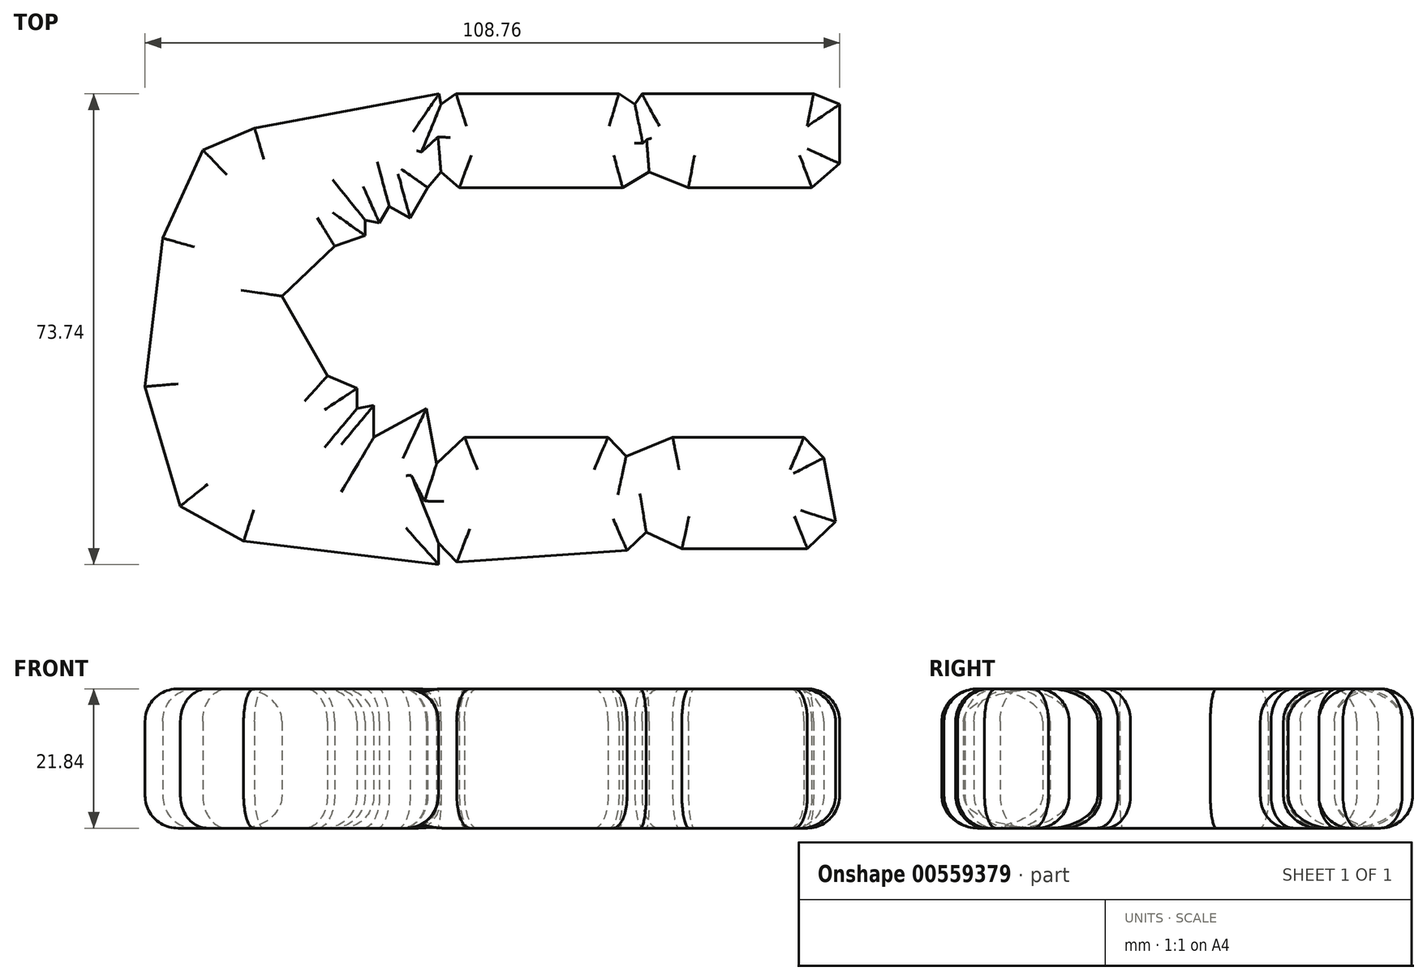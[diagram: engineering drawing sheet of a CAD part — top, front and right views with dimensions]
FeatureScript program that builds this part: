
annotation { "Feature Type Name" : "Feature", "Feature Type Description" : "" }
export const myFeature = defineFeature(function(context is Context, id is Id, definition is map)
    precondition{}
    {
        {
            var Q0;
            Q0=qCreatedBy(makeId("Top.planeOp"),FACE);
            var sketch = newSketch(context, id + "F0", { "sketchPlane" : qUnion([Q0])});
            skLineSegment(sketch, "E0", {"start": v(-56.88, -14.18) * mm, "end": v(-54.1, 9.09) * mm});
            skLineSegment(sketch, "E1", {"start": v(-54.1, 9.09) * mm, "end": v(-47.85, 22.91) * mm});
            skLineSegment(sketch, "E2", {"start": v(-47.85, 22.91) * mm, "end": v(-39.72, 26.3) * mm});
            skLineSegment(sketch, "E3", {"start": v(-39.72, 26.3) * mm, "end": v(-10.85, 31.7) * mm});
            skLineSegment(sketch, "E4", {"start": v(-10.85, 31.7) * mm, "end": v(-10.54, 30.04) * mm});
            skLineSegment(sketch, "E5", {"start": v(-10.54, 30.04) * mm, "end": v(-8.16, 31.7) * mm});
            skLineSegment(sketch, "E6", {"start": v(-8.16, 31.7) * mm, "end": v(17.31, 31.7) * mm});
            skLineSegment(sketch, "E7", {"start": v(17.31, 31.7) * mm, "end": v(19.83, 30.04) * mm});
            skLineSegment(sketch, "E8", {"start": v(19.83, 30.04) * mm, "end": v(20.93, 31.7) * mm});
            skLineSegment(sketch, "E9", {"start": v(20.93, 31.7) * mm, "end": v(47.8, 31.7) * mm});
            skLineSegment(sketch, "E10", {"start": v(47.8, 31.7) * mm, "end": v(51.88, 30.04) * mm});
            skLineSegment(sketch, "E11", {"start": v(51.88, 30.04) * mm, "end": v(51.88, 25.6) * mm});
            skLineSegment(sketch, "E12", {"start": v(51.88, 25.6) * mm, "end": v(51.88, 20.77) * mm});
            skLineSegment(sketch, "E13", {"start": v(51.88, 20.77) * mm, "end": v(47.52, 17) * mm});
            skLineSegment(sketch, "E14", {"start": v(47.52, 17) * mm, "end": v(30.33, 17) * mm});
            skLineSegment(sketch, "E15", {"start": v(30.33, 17) * mm, "end": v(28.2, 17) * mm});
            skLineSegment(sketch, "E16", {"start": v(28.2, 17) * mm, "end": v(22.05, 19.44) * mm});
            skLineSegment(sketch, "E17", {"start": v(22.05, 19.44) * mm, "end": v(17.9, 17) * mm});
            skLineSegment(sketch, "E18", {"start": v(17.9, 17) * mm, "end": v(-7.66, 17) * mm});
            skLineSegment(sketch, "E19", {"start": v(-7.66, 17) * mm, "end": v(-10.54, 19.44) * mm});
            skLineSegment(sketch, "E20", {"start": v(-10.54, 19.44) * mm, "end": v(-12.61, 17) * mm});
            skLineSegment(sketch, "E21", {"start": v(-12.61, 17) * mm, "end": v(-15.36, 12.2) * mm});
            skLineSegment(sketch, "E22", {"start": v(-15.36, 12.2) * mm, "end": v(-18.64, 14.09) * mm});
            skLineSegment(sketch, "E23", {"start": v(-18.64, 14.09) * mm, "end": v(-20.16, 11.44) * mm});
            skLineSegment(sketch, "E24", {"start": v(-20.16, 11.44) * mm, "end": v(-22.43, 11.93) * mm});
            skLineSegment(sketch, "E25", {"start": v(-22.43, 11.93) * mm, "end": v(-22.43, 9.5) * mm});
            skLineSegment(sketch, "E26", {"start": v(-22.43, 9.5) * mm, "end": v(-27.2, 7.83) * mm});
            skLineSegment(sketch, "E27", {"start": v(-27.2, 7.83) * mm, "end": v(-35.44, 0) * mm});
            skLineSegment(sketch, "E28", {"start": v(-35.44, 0) * mm, "end": v(-28.33, -12.5) * mm});
            skLineSegment(sketch, "E29", {"start": v(-28.33, -12.5) * mm, "end": v(-23.7, -14.47) * mm});
            skLineSegment(sketch, "E30", {"start": v(-23.7, -14.47) * mm, "end": v(-23.7, -17.62) * mm});
            skLineSegment(sketch, "E31", {"start": v(-23.7, -17.62) * mm, "end": v(-21.06, -17.12) * mm});
            skLineSegment(sketch, "E32", {"start": v(-21.06, -17.12) * mm, "end": v(-21.06, -22.11) * mm});
            skLineSegment(sketch, "E33", {"start": v(-21.06, -22.11) * mm, "end": v(-12.82, -17.62) * mm});
            skLineSegment(sketch, "E34", {"start": v(-12.82, -17.62) * mm, "end": v(-11.2, -26.25) * mm});
            skLineSegment(sketch, "E35", {"start": v(-11.2, -26.25) * mm, "end": v(-6.86, -22.11) * mm});
            skLineSegment(sketch, "E36", {"start": v(-6.86, -22.11) * mm, "end": v(15.61, -22.11) * mm});
            skLineSegment(sketch, "E37", {"start": v(15.61, -22.11) * mm, "end": v(18.45, -25.1) * mm});
            skLineSegment(sketch, "E38", {"start": v(18.45, -25.1) * mm, "end": v(25.74, -22.11) * mm});
            skLineSegment(sketch, "E39", {"start": v(25.74, -22.11) * mm, "end": v(46.3, -22.11) * mm});
            skLineSegment(sketch, "E40", {"start": v(46.3, -22.11) * mm, "end": v(49.4, -25.36) * mm});
            skLineSegment(sketch, "E41", {"start": v(49.4, -25.36) * mm, "end": v(51.26, -35.35) * mm});
            skLineSegment(sketch, "E42", {"start": v(51.26, -35.35) * mm, "end": v(46.82, -39.57) * mm});
            skLineSegment(sketch, "E43", {"start": v(46.82, -39.57) * mm, "end": v(27.19, -39.57) * mm});
            skLineSegment(sketch, "E44", {"start": v(27.19, -39.57) * mm, "end": v(21.6, -37) * mm});
            skLineSegment(sketch, "E45", {"start": v(21.6, -37) * mm, "end": v(18.6, -39.86) * mm});
            skLineSegment(sketch, "E46", {"start": v(18.6, -39.86) * mm, "end": v(-8.07, -41.7) * mm});
            skLineSegment(sketch, "E47", {"start": v(-8.07, -41.7) * mm, "end": v(-10.94, -38.67) * mm});
            skLineSegment(sketch, "E48", {"start": v(-10.94, -38.67) * mm, "end": v(-10.94, -42.04) * mm});
            skLineSegment(sketch, "E49", {"start": v(-10.94, -42.04) * mm, "end": v(-41.44, -38.4) * mm});
            skLineSegment(sketch, "E50", {"start": v(-41.44, -38.4) * mm, "end": v(-51.35, -32.9) * mm});
            skLineSegment(sketch, "E51", {"start": v(-51.35, -32.9) * mm, "end": v(-56.88, -14.18) * mm});
            skSolve(sketch);
        }
        {
            var Q0;
            Q0 = qSketchRegion(id + "F0", true);
            extrude(context, id + "F1", {"entities" : qUnion([Q0]), "depth" : 21.84 * mm, "offsetDistance" : 25.4 * mm});
        }
        {
            var Q0;
            Q0=makeQuery(id+"F1.opExtrude","CAP_FACE",FACE,{"disambiguationData":[OSD([sQuery(id+"F0.wireOp",EDGE,"E0"),sQuery(id+"F0.wireOp",EDGE,"E1"),sQuery(id+"F0.wireOp",EDGE,"E2"),sQuery(id+"F0.wireOp",EDGE,"E3"),sQuery(id+"F0.wireOp",EDGE,"E4"),sQuery(id+"F0.wireOp",EDGE,"E5"),sQuery(id+"F0.wireOp",EDGE,"E6"),sQuery(id+"F0.wireOp",EDGE,"E7"),sQuery(id+"F0.wireOp",EDGE,"E8"),sQuery(id+"F0.wireOp",EDGE,"E9"),sQuery(id+"F0.wireOp",EDGE,"E10"),sQuery(id+"F0.wireOp",EDGE,"E11"),sQuery(id+"F0.wireOp",EDGE,"E12"),sQuery(id+"F0.wireOp",EDGE,"E13"),sQuery(id+"F0.wireOp",EDGE,"E14"),sQuery(id+"F0.wireOp",EDGE,"E15"),sQuery(id+"F0.wireOp",EDGE,"E16"),sQuery(id+"F0.wireOp",EDGE,"E17"),sQuery(id+"F0.wireOp",EDGE,"E18"),sQuery(id+"F0.wireOp",EDGE,"E19"),sQuery(id+"F0.wireOp",EDGE,"E20"),sQuery(id+"F0.wireOp",EDGE,"E21"),sQuery(id+"F0.wireOp",EDGE,"E22"),sQuery(id+"F0.wireOp",EDGE,"E23"),sQuery(id+"F0.wireOp",EDGE,"E24"),sQuery(id+"F0.wireOp",EDGE,"E25"),sQuery(id+"F0.wireOp",EDGE,"E26"),sQuery(id+"F0.wireOp",EDGE,"E27"),sQuery(id+"F0.wireOp",EDGE,"E28"),sQuery(id+"F0.wireOp",EDGE,"E29"),sQuery(id+"F0.wireOp",EDGE,"E30"),sQuery(id+"F0.wireOp",EDGE,"E31"),sQuery(id+"F0.wireOp",EDGE,"E32"),sQuery(id+"F0.wireOp",EDGE,"E33"),sQuery(id+"F0.wireOp",EDGE,"E34"),sQuery(id+"F0.wireOp",EDGE,"E35"),sQuery(id+"F0.wireOp",EDGE,"E36"),sQuery(id+"F0.wireOp",EDGE,"E37"),sQuery(id+"F0.wireOp",EDGE,"E38"),sQuery(id+"F0.wireOp",EDGE,"E39"),sQuery(id+"F0.wireOp",EDGE,"E40"),sQuery(id+"F0.wireOp",EDGE,"E41"),sQuery(id+"F0.wireOp",EDGE,"E42"),sQuery(id+"F0.wireOp",EDGE,"E43"),sQuery(id+"F0.wireOp",EDGE,"E44"),sQuery(id+"F0.wireOp",EDGE,"E45"),sQuery(id+"F0.wireOp",EDGE,"E46"),sQuery(id+"F0.wireOp",EDGE,"E47"),sQuery(id+"F0.wireOp",EDGE,"E48"),sQuery(id+"F0.wireOp",EDGE,"E49"),sQuery(id+"F0.wireOp",EDGE,"E50"),sQuery(id+"F0.wireOp",EDGE,"E51")])],"isStart":false});
            fillet(context, id + "F2", {"entities" : qUnion([Q0]), "radius" : 5.08 * mm, "tangentPropagation" : true, "allowEdgeOverflow" : false});
        }
        {
            var Q0;
            Q0=makeQuery(id+"F1.opExtrude","CAP_FACE",FACE,{"disambiguationData":[OSD([sQuery(id+"F0.wireOp",EDGE,"E0"),sQuery(id+"F0.wireOp",EDGE,"E1"),sQuery(id+"F0.wireOp",EDGE,"E2"),sQuery(id+"F0.wireOp",EDGE,"E3"),sQuery(id+"F0.wireOp",EDGE,"E4"),sQuery(id+"F0.wireOp",EDGE,"E5"),sQuery(id+"F0.wireOp",EDGE,"E6"),sQuery(id+"F0.wireOp",EDGE,"E7"),sQuery(id+"F0.wireOp",EDGE,"E8"),sQuery(id+"F0.wireOp",EDGE,"E9"),sQuery(id+"F0.wireOp",EDGE,"E10"),sQuery(id+"F0.wireOp",EDGE,"E11"),sQuery(id+"F0.wireOp",EDGE,"E12"),sQuery(id+"F0.wireOp",EDGE,"E13"),sQuery(id+"F0.wireOp",EDGE,"E14"),sQuery(id+"F0.wireOp",EDGE,"E15"),sQuery(id+"F0.wireOp",EDGE,"E16"),sQuery(id+"F0.wireOp",EDGE,"E17"),sQuery(id+"F0.wireOp",EDGE,"E18"),sQuery(id+"F0.wireOp",EDGE,"E19"),sQuery(id+"F0.wireOp",EDGE,"E20"),sQuery(id+"F0.wireOp",EDGE,"E21"),sQuery(id+"F0.wireOp",EDGE,"E22"),sQuery(id+"F0.wireOp",EDGE,"E23"),sQuery(id+"F0.wireOp",EDGE,"E24"),sQuery(id+"F0.wireOp",EDGE,"E25"),sQuery(id+"F0.wireOp",EDGE,"E26"),sQuery(id+"F0.wireOp",EDGE,"E27"),sQuery(id+"F0.wireOp",EDGE,"E28"),sQuery(id+"F0.wireOp",EDGE,"E29"),sQuery(id+"F0.wireOp",EDGE,"E30"),sQuery(id+"F0.wireOp",EDGE,"E31"),sQuery(id+"F0.wireOp",EDGE,"E32"),sQuery(id+"F0.wireOp",EDGE,"E33"),sQuery(id+"F0.wireOp",EDGE,"E34"),sQuery(id+"F0.wireOp",EDGE,"E35"),sQuery(id+"F0.wireOp",EDGE,"E36"),sQuery(id+"F0.wireOp",EDGE,"E37"),sQuery(id+"F0.wireOp",EDGE,"E38"),sQuery(id+"F0.wireOp",EDGE,"E39"),sQuery(id+"F0.wireOp",EDGE,"E40"),sQuery(id+"F0.wireOp",EDGE,"E41"),sQuery(id+"F0.wireOp",EDGE,"E42"),sQuery(id+"F0.wireOp",EDGE,"E43"),sQuery(id+"F0.wireOp",EDGE,"E44"),sQuery(id+"F0.wireOp",EDGE,"E45"),sQuery(id+"F0.wireOp",EDGE,"E46"),sQuery(id+"F0.wireOp",EDGE,"E47"),sQuery(id+"F0.wireOp",EDGE,"E48"),sQuery(id+"F0.wireOp",EDGE,"E49"),sQuery(id+"F0.wireOp",EDGE,"E50"),sQuery(id+"F0.wireOp",EDGE,"E51")])],"isStart":true});
            fillet(context, id + "F3", {"entities" : qUnion([Q0]), "radius" : 5.08 * mm, "tangentPropagation" : true, "allowEdgeOverflow" : false});
        }
    });
